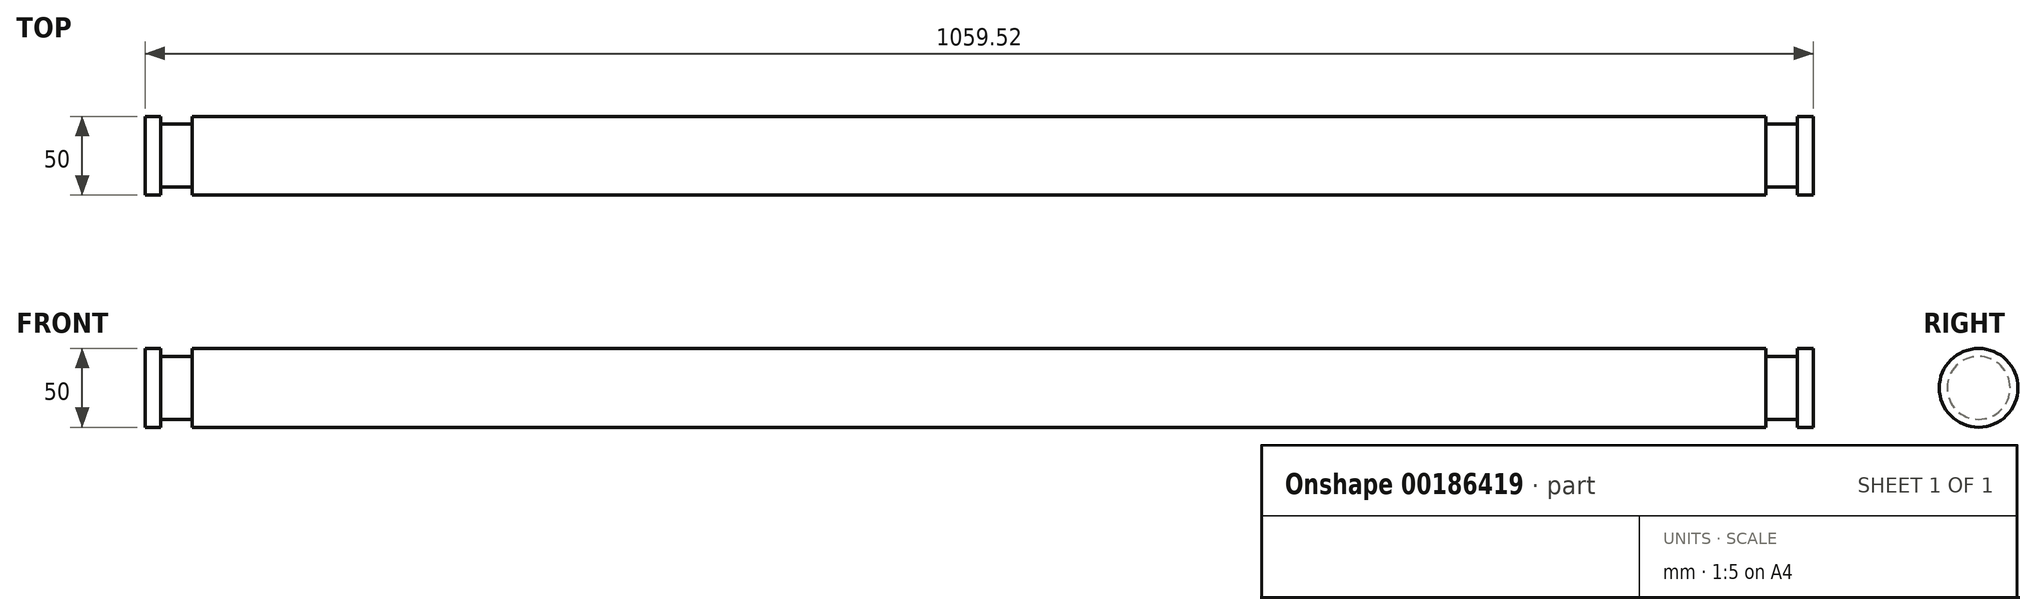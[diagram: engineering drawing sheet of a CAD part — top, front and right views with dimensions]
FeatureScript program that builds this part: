
annotation { "Feature Type Name" : "Feature", "Feature Type Description" : "" }
export const myFeature = defineFeature(function(context is Context, id is Id, definition is map)
    precondition{}
    {
        {
            var Q0;
            Q0=qCreatedBy(makeId("Front.planeOp"),FACE);
            var sketch = newSketch(context, id + "F0", { "sketchPlane" : qUnion([Q0])});
            skLineSegment(sketch, "E0", {"start": v(0, 0) * mm, "end": v(1059.52, 0) * mm});
            skLineSegment(sketch, "E1", {"start": v(1059.52, 0) * mm, "end": v(1059.52, 25) * mm});
            skLineSegment(sketch, "E2", {"start": v(1029.52, 20) * mm, "end": v(1029.52, 25) * mm});
            skLineSegment(sketch, "E3", {"start": v(1029.52, 25) * mm, "end": v(30, 25) * mm});
            skLineSegment(sketch, "E4", {"start": v(30, 25) * mm, "end": v(30, 20) * mm});
            skLineSegment(sketch, "E5", {"start": v(0, 25) * mm, "end": v(0, 0) * mm});
            skLineSegment(sketch, "E6", {"start": v(1029.52, 20) * mm, "end": v(1049.52, 20) * mm});
            skLineSegment(sketch, "E7", {"start": v(1049.52, 20) * mm, "end": v(1049.52, 25) * mm});
            skLineSegment(sketch, "E8", {"start": v(1049.52, 25) * mm, "end": v(1059.52, 25) * mm});
            skLineSegment(sketch, "E9", {"start": v(30, 20) * mm, "end": v(10, 20) * mm});
            skLineSegment(sketch, "E10", {"start": v(10, 20) * mm, "end": v(10, 25) * mm});
            skLineSegment(sketch, "E11", {"start": v(10, 25) * mm, "end": v(0, 25) * mm});
            skSolve(sketch);
        }
        {
            var Q0;
            Q0=qSketchRegion(id+"F0",true);
            var Q1;
            Q1=sQuery(id+"F0.wireOp",EDGE,"E0");
            revolve(context, id + "F1", {"entities" : qUnion([Q0]), "axis" : qUnion([Q1]), "revolveType" : RevolveType.FULL});
        }
    });
